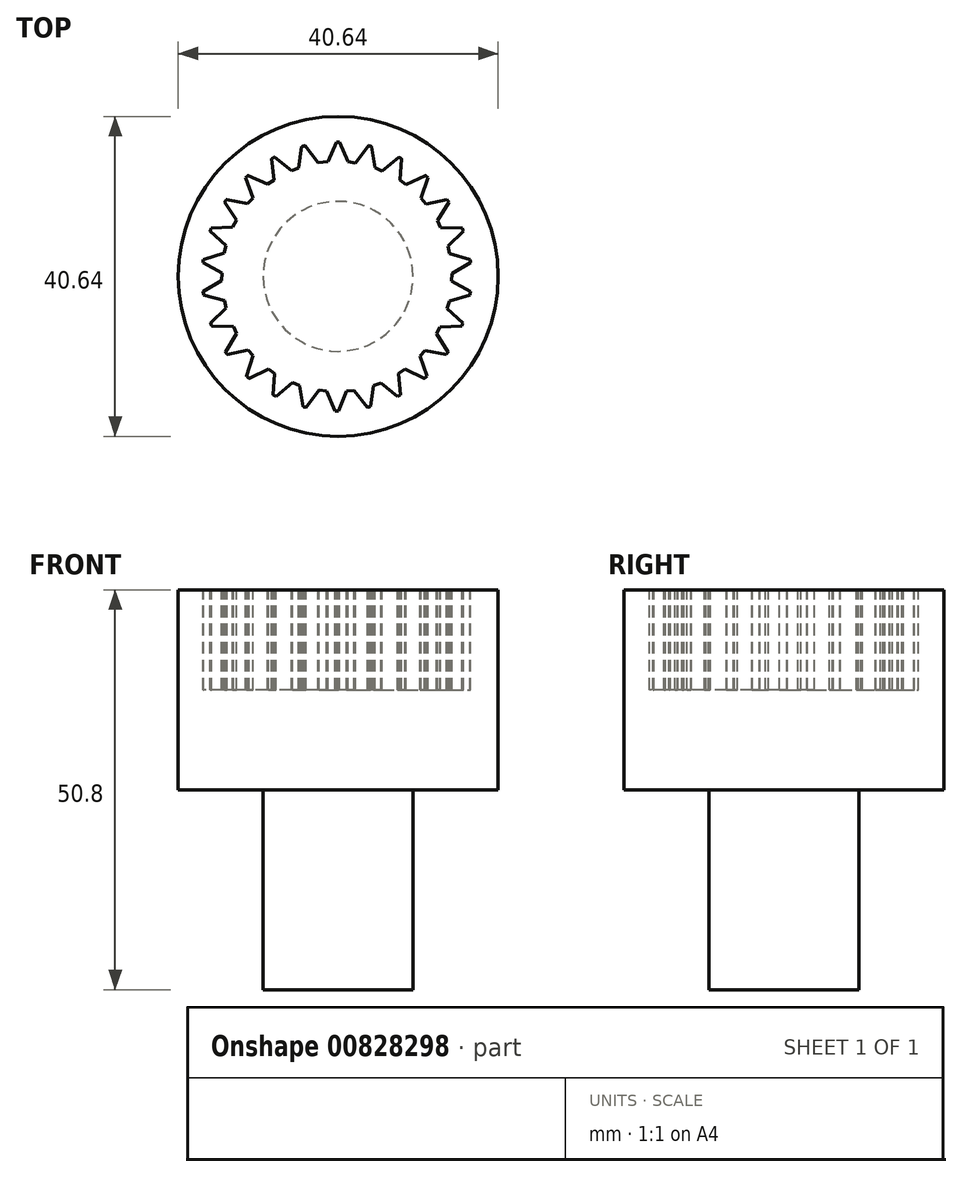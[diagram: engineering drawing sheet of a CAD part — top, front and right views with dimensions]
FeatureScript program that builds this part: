
annotation { "Feature Type Name" : "Feature", "Feature Type Description" : "" }
export const myFeature = defineFeature(function(context is Context, id is Id, definition is map)
    precondition{}
    {
        {
            var Q0;
            Q0=qCreatedBy(makeId("Top.planeOp"),FACE);
            var sketch = newSketch(context, id + "F0", { "sketchPlane" : qUnion([Q0])});
            skCircle(sketch, "E0", {"center": v(0, 0) * mm, "radius": 20.32 * mm});
            skSolve(sketch);
        }
        {
            var Q0;
            Q0=makeQuery(id+"F0.imprint","IMPRINT",FACE,{"disambiguationData":[TD([[makeQuery(id+"F0.imprint","IMPRINT",EDGE,{"derivedFrom":sQuery(id+"F0.wireOp",EDGE,"E0")}),1.0]])]});
            extrude(context, id + "F1", {"entities" : qUnion([Q0]), "depth" : 25.4 * mm, "offsetDistance" : 25.4 * mm});
        }
        {
            var Q0;
            Q0=makeQuery(id+"F1.opExtrude","CAP_FACE",FACE,{"disambiguationData":[OSD([sQuery(id+"F0.wireOp",EDGE,"E0")])],"isStart":false});
            var sketch = newSketch(context, id + "F2", { "sketchPlane" : qUnion([Q0])});
            skArc(sketch, "E1", {"start": v(0.2, 17.07) * mm, "mid": v(0, 17.07) * mm, "end": v(-0.2, 17.07) * mm});
            skLineSegment(sketch, "E2", {"start": v(1.27, 14.55) * mm, "end": v(0.2, 17.07) * mm});
            skLineSegment(sketch, "E3", {"start": v(-1.27, 14.55) * mm, "end": v(-0.2, 17.07) * mm});
            skLineSegment(sketch, "E4.1.0", {"start": v(4.7, 13.78) * mm, "end": v(4.27, 16.48) * mm});
            skArc(sketch, "E4.1.1", {"start": v(4.27, 16.48) * mm, "mid": v(4.07, 16.53) * mm, "end": v(3.87, 16.58) * mm});
            skLineSegment(sketch, "E4.1.2", {"start": v(2.24, 14.39) * mm, "end": v(3.87, 16.58) * mm});
            skLineSegment(sketch, "E4.2.0", {"start": v(7.85, 12.22) * mm, "end": v(8.07, 14.95) * mm});
            skArc(sketch, "E4.2.1", {"start": v(8.07, 14.95) * mm, "mid": v(7.9, 15.04) * mm, "end": v(7.71, 15.14) * mm});
            skLineSegment(sketch, "E4.2.2", {"start": v(5.6, 13.4) * mm, "end": v(7.71, 15.14) * mm});
            skLineSegment(sketch, "E4.3.0", {"start": v(10.54, 9.95) * mm, "end": v(11.4, 12.55) * mm});
            skArc(sketch, "E4.3.1", {"start": v(11.4, 12.55) * mm, "mid": v(11.25, 12.68) * mm, "end": v(11.1, 12.82) * mm});
            skLineSegment(sketch, "E4.3.2", {"start": v(8.63, 11.63) * mm, "end": v(11.1, 12.82) * mm});
            skLineSegment(sketch, "E4.4.0", {"start": v(12.6, 7.1) * mm, "end": v(14.07, 9.42) * mm});
            skArc(sketch, "E4.4.1", {"start": v(14.07, 9.42) * mm, "mid": v(13.95, 9.59) * mm, "end": v(13.83, 9.76) * mm});
            skLineSegment(sketch, "E4.4.2", {"start": v(11.16, 9.2) * mm, "end": v(13.83, 9.76) * mm});
            skLineSegment(sketch, "E4.5.0", {"start": v(13.94, 3.85) * mm, "end": v(15.9, 5.75) * mm});
            skArc(sketch, "E4.5.1", {"start": v(15.9, 5.75) * mm, "mid": v(15.83, 5.94) * mm, "end": v(15.76, 6.13) * mm});
            skLineSegment(sketch, "E4.5.2", {"start": v(13.03, 6.22) * mm, "end": v(15.76, 6.13) * mm});
            skLineSegment(sketch, "E4.6.0", {"start": v(14.45, 0.37) * mm, "end": v(16.82, 1.75) * mm});
            skArc(sketch, "E4.6.1", {"start": v(16.82, 1.75) * mm, "mid": v(16.8, 1.95) * mm, "end": v(16.77, 2.15) * mm});
            skLineSegment(sketch, "E4.6.2", {"start": v(14.13, 2.9) * mm, "end": v(16.77, 2.15) * mm});
            skLineSegment(sketch, "E4.7.0", {"start": v(14.12, -3.13) * mm, "end": v(16.75, -2.36) * mm});
            skArc(sketch, "E4.7.1", {"start": v(16.75, -2.36) * mm, "mid": v(16.77, -2.15) * mm, "end": v(16.8, -1.95) * mm});
            skLineSegment(sketch, "E4.7.2", {"start": v(14.42, -0.6) * mm, "end": v(16.8, -1.95) * mm});
            skLineSegment(sketch, "E4.8.0", {"start": v(12.97, -6.45) * mm, "end": v(15.7, -6.33) * mm});
            skArc(sketch, "E4.8.1", {"start": v(15.7, -6.33) * mm, "mid": v(15.77, -6.14) * mm, "end": v(15.84, -5.94) * mm});
            skLineSegment(sketch, "E4.8.2", {"start": v(13.85, -4.07) * mm, "end": v(15.84, -5.94) * mm});
            skLineSegment(sketch, "E4.9.0", {"start": v(11.05, -9.4) * mm, "end": v(13.74, -9.93) * mm});
            skArc(sketch, "E4.9.1", {"start": v(13.74, -9.93) * mm, "mid": v(13.85, -9.76) * mm, "end": v(13.96, -9.6) * mm});
            skLineSegment(sketch, "E4.9.2", {"start": v(12.48, -7.3) * mm, "end": v(13.96, -9.6) * mm});
            skLineSegment(sketch, "E4.10.0", {"start": v(8.5, -11.8) * mm, "end": v(10.97, -12.96) * mm});
            skArc(sketch, "E4.10.1", {"start": v(10.97, -12.96) * mm, "mid": v(11.12, -12.83) * mm, "end": v(11.27, -12.7) * mm});
            skLineSegment(sketch, "E4.10.2", {"start": v(10.38, -10.1) * mm, "end": v(11.27, -12.7) * mm});
            skLineSegment(sketch, "E4.11.0", {"start": v(5.43, -13.53) * mm, "end": v(7.56, -15.25) * mm});
            skArc(sketch, "E4.11.1", {"start": v(7.56, -15.25) * mm, "mid": v(7.74, -15.15) * mm, "end": v(7.92, -15.06) * mm});
            skLineSegment(sketch, "E4.11.2", {"start": v(7.67, -12.33) * mm, "end": v(7.92, -15.06) * mm});
            skLineSegment(sketch, "E4.12.0", {"start": v(2.04, -14.48) * mm, "end": v(3.7, -16.65) * mm});
            skArc(sketch, "E4.12.1", {"start": v(3.7, -16.65) * mm, "mid": v(3.9, -16.6) * mm, "end": v(4.1, -16.55) * mm});
            skLineSegment(sketch, "E4.12.2", {"start": v(4.5, -13.85) * mm, "end": v(4.1, -16.55) * mm});
            skLineSegment(sketch, "E4.13.0", {"start": v(-1.47, -14.6) * mm, "end": v(-0.38, -17.1) * mm});
            skArc(sketch, "E4.13.1", {"start": v(-0.38, -17.1) * mm, "mid": v(-0.18, -17.1) * mm, "end": v(0.03, -17.1) * mm});
            skLineSegment(sketch, "E4.13.2", {"start": v(1.07, -14.57) * mm, "end": v(0.03, -17.1) * mm});
            skLineSegment(sketch, "E4.14.0", {"start": v(-4.91, -13.86) * mm, "end": v(-4.45, -16.56) * mm});
            skArc(sketch, "E4.14.1", {"start": v(-4.45, -16.56) * mm, "mid": v(-4.25, -16.6) * mm, "end": v(-4.05, -16.65) * mm});
            skLineSegment(sketch, "E4.14.2", {"start": v(-2.44, -14.44) * mm, "end": v(-4.05, -16.65) * mm});
            skLineSegment(sketch, "E4.15.0", {"start": v(-8.08, -12.33) * mm, "end": v(-8.27, -15.06) * mm});
            skArc(sketch, "E4.15.1", {"start": v(-8.27, -15.06) * mm, "mid": v(-8.1, -15.15) * mm, "end": v(-7.91, -15.25) * mm});
            skLineSegment(sketch, "E4.15.2", {"start": v(-5.82, -13.49) * mm, "end": v(-7.91, -15.25) * mm});
            skLineSegment(sketch, "E4.16.0", {"start": v(-10.8, -10.1) * mm, "end": v(-11.63, -12.7) * mm});
            skArc(sketch, "E4.16.1", {"start": v(-11.63, -12.7) * mm, "mid": v(-11.47, -12.83) * mm, "end": v(-11.32, -12.96) * mm});
            skLineSegment(sketch, "E4.16.2", {"start": v(-8.87, -11.75) * mm, "end": v(-11.32, -12.96) * mm});
            skLineSegment(sketch, "E4.17.0", {"start": v(-12.89, -7.27) * mm, "end": v(-14.32, -9.6) * mm});
            skArc(sketch, "E4.17.1", {"start": v(-14.32, -9.6) * mm, "mid": v(-14.2, -9.77) * mm, "end": v(-14.09, -9.93) * mm});
            skLineSegment(sketch, "E4.17.2", {"start": v(-11.42, -9.34) * mm, "end": v(-14.09, -9.93) * mm});
            skLineSegment(sketch, "E4.18.0", {"start": v(-14.25, -4.03) * mm, "end": v(-16.2, -5.95) * mm});
            skArc(sketch, "E4.18.1", {"start": v(-16.2, -5.95) * mm, "mid": v(-16.13, -6.14) * mm, "end": v(-16.05, -6.33) * mm});
            skLineSegment(sketch, "E4.18.2", {"start": v(-13.32, -6.4) * mm, "end": v(-16.05, -6.33) * mm});
            skLineSegment(sketch, "E4.19.0", {"start": v(-14.8, -0.56) * mm, "end": v(-17.15, -1.96) * mm});
            skArc(sketch, "E4.19.1", {"start": v(-17.15, -1.96) * mm, "mid": v(-17.13, -2.16) * mm, "end": v(-17.1, -2.36) * mm});
            skLineSegment(sketch, "E4.19.2", {"start": v(-14.46, -3.07) * mm, "end": v(-17.1, -2.36) * mm});
            skLineSegment(sketch, "E4.20.0", {"start": v(-14.51, 2.95) * mm, "end": v(-17.13, 2.15) * mm});
            skArc(sketch, "E4.20.1", {"start": v(-17.13, 2.15) * mm, "mid": v(-17.15, 1.95) * mm, "end": v(-17.17, 1.75) * mm});
            skLineSegment(sketch, "E4.20.2", {"start": v(-14.78, 0.42) * mm, "end": v(-17.17, 1.75) * mm});
            skLineSegment(sketch, "E4.21.0", {"start": v(-13.4, 6.28) * mm, "end": v(-16.12, 6.13) * mm});
            skArc(sketch, "E4.21.1", {"start": v(-16.12, 6.13) * mm, "mid": v(-16.2, 5.94) * mm, "end": v(-16.26, 5.75) * mm});
            skLineSegment(sketch, "E4.21.2", {"start": v(-14.25, 3.9) * mm, "end": v(-16.26, 5.75) * mm});
            skLineSegment(sketch, "E4.22.0", {"start": v(-11.5, 9.25) * mm, "end": v(-14.2, 9.76) * mm});
            skArc(sketch, "E4.22.1", {"start": v(-14.2, 9.76) * mm, "mid": v(-14.3, 9.59) * mm, "end": v(-14.42, 9.42) * mm});
            skLineSegment(sketch, "E4.22.2", {"start": v(-12.91, 7.14) * mm, "end": v(-14.42, 9.42) * mm});
            skLineSegment(sketch, "E4.23.0", {"start": v(-8.97, 11.69) * mm, "end": v(-11.46, 12.82) * mm});
            skArc(sketch, "E4.23.1", {"start": v(-11.46, 12.82) * mm, "mid": v(-11.61, 12.68) * mm, "end": v(-11.76, 12.54) * mm});
            skLineSegment(sketch, "E4.23.2", {"start": v(-10.84, 9.97) * mm, "end": v(-11.76, 12.54) * mm});
            skLineSegment(sketch, "E4.24.0", {"start": v(-5.93, 13.45) * mm, "end": v(-8.07, 15.14) * mm});
            skArc(sketch, "E4.24.1", {"start": v(-8.07, 15.14) * mm, "mid": v(-8.25, 15.04) * mm, "end": v(-8.43, 14.94) * mm});
            skLineSegment(sketch, "E4.24.2", {"start": v(-8.15, 12.22) * mm, "end": v(-8.43, 14.94) * mm});
            skLineSegment(sketch, "E4.25.0", {"start": v(-2.55, 14.43) * mm, "end": v(-4.23, 16.58) * mm});
            skArc(sketch, "E4.25.1", {"start": v(-4.23, 16.58) * mm, "mid": v(-4.43, 16.53) * mm, "end": v(-4.62, 16.48) * mm});
            skLineSegment(sketch, "E4.25.2", {"start": v(-5, 13.77) * mm, "end": v(-4.62, 16.48) * mm});
            skPoint(sketch, "E4.center", {"position": v(-0.18, -0.01) * mm});
            skLineSegment(sketch, "E4.anchor1", {"start": v(-0.18, -0.01) * mm, "end": v(-1.27, 14.55) * mm, "construction": true});
            skLineSegment(sketch, "E4.anchor2", {"start": v(-0.18, -0.01) * mm, "end": v(-5, 13.77) * mm, "construction": true});
            skLineSegment(sketch, "E5", {"start": v(-5, 13.77) * mm, "end": v(-5.93, 13.45) * mm});
            skLineSegment(sketch, "E6", {"start": v(-8.15, 12.22) * mm, "end": v(-8.97, 11.69) * mm});
            skLineSegment(sketch, "E7", {"start": v(-1.27, 14.55) * mm, "end": v(-2.55, 14.43) * mm});
            skLineSegment(sketch, "E8", {"start": v(2.24, 14.39) * mm, "end": v(1.27, 14.55) * mm});
            skLineSegment(sketch, "E9", {"start": v(5.6, 13.4) * mm, "end": v(4.7, 13.78) * mm});
            skLineSegment(sketch, "E10", {"start": v(8.63, 11.63) * mm, "end": v(7.85, 12.22) * mm});
            skLineSegment(sketch, "E11", {"start": v(11.16, 9.2) * mm, "end": v(10.54, 9.95) * mm});
            skLineSegment(sketch, "E12", {"start": v(-10.84, 9.97) * mm, "end": v(-11.5, 9.25) * mm});
            skLineSegment(sketch, "E13", {"start": v(-14.25, 3.9) * mm, "end": v(-14.51, 2.95) * mm});
            skLineSegment(sketch, "E14", {"start": v(-14.78, 0.42) * mm, "end": v(-14.8, -0.56) * mm});
            skLineSegment(sketch, "E15", {"start": v(-14.46, -3.07) * mm, "end": v(-14.25, -4.03) * mm});
            skLineSegment(sketch, "E16", {"start": v(-13.32, -6.4) * mm, "end": v(-12.89, -7.27) * mm});
            skLineSegment(sketch, "E17", {"start": v(-11.42, -9.34) * mm, "end": v(-10.8, -10.1) * mm});
            skLineSegment(sketch, "E18", {"start": v(-8.87, -11.75) * mm, "end": v(-8.08, -12.33) * mm});
            skLineSegment(sketch, "E19", {"start": v(-5.82, -13.49) * mm, "end": v(-4.91, -13.86) * mm});
            skLineSegment(sketch, "E20", {"start": v(-2.44, -14.44) * mm, "end": v(-1.47, -14.6) * mm});
            skLineSegment(sketch, "E21", {"start": v(1.07, -14.57) * mm, "end": v(2.04, -14.48) * mm});
            skLineSegment(sketch, "E22", {"start": v(4.5, -13.85) * mm, "end": v(5.43, -13.53) * mm});
            skLineSegment(sketch, "E23", {"start": v(7.67, -12.33) * mm, "end": v(8.5, -11.8) * mm});
            skLineSegment(sketch, "E24", {"start": v(10.38, -10.1) * mm, "end": v(11.05, -9.4) * mm});
            skLineSegment(sketch, "E25", {"start": v(12.48, -7.3) * mm, "end": v(12.97, -6.45) * mm});
            skLineSegment(sketch, "E26", {"start": v(13.85, -4.07) * mm, "end": v(14.12, -3.13) * mm});
            skLineSegment(sketch, "E27", {"start": v(14.42, -0.6) * mm, "end": v(14.45, 0.37) * mm});
            skLineSegment(sketch, "E28", {"start": v(-13.4, 6.28) * mm, "end": v(-12.91, 7.14) * mm});
            skLineSegment(sketch, "E29", {"start": v(14.13, 2.9) * mm, "end": v(13.94, 3.85) * mm});
            skLineSegment(sketch, "E30", {"start": v(13.03, 6.22) * mm, "end": v(12.6, 7.1) * mm});
            skSolve(sketch);
        }
        {
            var Q0;
            Q0 = qSketchRegion(id + "F2", true);
            extrude(context, id + "F3", {"entities" : qUnion([Q0]), "operationType" : NewBodyOperationType.REMOVE, "oppositeDirection" : true, "depth" : 12.7 * mm, "offsetDistance" : 25.4 * mm});
        }
        {
            var Q0;
            Q0=makeQuery(id+"F1.opExtrude","CAP_FACE",FACE,{"disambiguationData":[OSD([sQuery(id+"F0.wireOp",EDGE,"E0")])],"isStart":true});
            var sketch = newSketch(context, id + "F4", { "sketchPlane" : qUnion([Q0])});
            skCircle(sketch, "E31", {"center": v(0, 0) * mm, "radius": 9.52 * mm});
            skSolve(sketch);
        }
        {
            var Q0;
            Q0 = qSketchRegion(id + "F4", true);
            extrude(context, id + "F5", {"entities" : qUnion([Q0]), "operationType" : NewBodyOperationType.ADD, "depth" : 25.4 * mm, "offsetDistance" : 25.4 * mm});
        }
    });
